# Revit family: FOR UPDATE_36106USA_NEWцц
name_source: partatom
category: Plumbing Fixtures
revit_build: Autodesk Revit 2018 (Build: 20170223_1515(x64)
units: mm (PartAtom-declared; Revit-internal decimal feet)

## family parameters
Always vertical = No
Cut with Voids When Loaded = No
OmniClass Number = 23.31.11.00
OmniClass Title = Faucets
Part Type = Normal
Room Calculation Point = No
Round Connector Dimension = Use Diameter
Shared = No
Work Plane-Based = Yes

## types (2) — shared parameters
Always visible = Yes
BIMobject category = Taps & Mixers
Default Elevation = 1219.2 mm  [stored 4 ft]
Description = AXOR Citterio E Single lever basin mixer for concealed installation wall-mounted with pin handle, spout 221 mm and escutcheons
Design country = Germany
EAN code = 4011097777030
Edition number = 1
IFC Classification = Valve
Manufacturer = AXOR
Manufacturer country = Germany
Manufacturer name = AXOR
Model = 36106USA
OmniClass Code = 23-31 11 00
OmniClass Description = Faucets
Product Guid = 065ecfa4-e4c7-49cc-b21d-55c0eebbfcd6
Product SKU = 36106USA
Product data url = https://bimobject.com
Product family = AXOR Citterio E
Product group = Basin mixers
Product name = 36106USA AXOR Citterio E Single lever basin mixer for concealed installation wall-mounted with pin handle, spout 221 mm and escutcheons
QR code = https://bimobject.com
URL = https://www.axor-design.com
Weight Net (Kg) = 1.4

## per-type parameters (varying)
| type | Material 1 |
| 001 Chrome | AXOR - Metal - 001 Chrome |
| 671 Matt Black | AXOR - Metal - 671 Matt Black |

note: [stored X ft] marks values corroborated as IEEE doubles in the binary element streams (Revit-internal decimal feet)

## geometry (parser evidence)
native form markers: Sweep x1
no freeform markers — native parametric forms only
